# Revit family: EVID-S10.1D
name_source: partatom
category: Communication Devices
revit_build: Autodesk Revit 2017 (Build: 20160225_1515(x64)
units: mm (PartAtom-declared; Revit-internal decimal feet)

## family parameters
Always vertical = Yes
Cut with Voids When Loaded = No
Maintain Annotation Orientation = Yes
OmniClass Number = 23.85.10.11.11.21
OmniClass Title = Speakers
Part Type = Normal
Room Calculation Point = No
Round Connector Dimension = Use Diameter
Shared = No
Work Plane-Based = Yes

## types (2) — shared parameters
ArchitectsAndEngineersSpecs = https://www.electrovoice.com
Depth = 490.8 mm  [stored 1.61024 ft]
Description = Two 10 inch high-excursion woofers. Carefully engineered for outdoor environments (IP54 nad IP65), without compromising performance. 400 W power handling provides for 120 dB maximum SPL (126 dB peak). 70/100 V transformer input panel accessory available. Crossover input panel accessory available.
Disclaimer = http://resource.boschsecurity.com
Height = 360.5 mm  [stored 1.18274 ft]
IfcExportAs = IfcBuildingElementProxy
IfcExportType = IfcBuildingElementProxyType
InstallationManual = https://www.electrovoice.com
Length = 650.7 mm  [stored 2.13484 ft]
Manufacturer = Electro Voice
ManufacturerURL = https://www.electrovoice.com
PlanningTools = https://www.electrovoice.com
ProductInformation = https://www.electrovoice.com
Uniclass2015Code = Pr_60_75_08_02
Version = 1
zero-valued in all types: Default Elevation

## per-type parameters (varying)
| type | CTN | GrillMaterial | LoudspeakerMaterial | MaterialRALColour | ModelNumber |
| EVIDS10.1DB_Subwoofer_2x10"_Cabinet_Black | EVIDS10.1DB | 16GA Powder-coatedGalvanneal - B | 13-plyWeather-resistantBirchEVCoat -RAL9004 | RAL9004 | F.01U.332.744 |
| EVIDS10.1DW_Subwoofer_2x10"_Cabinet_White | EVIDS10.1DW | 16GA Powder-coatedGalvanneal - W | 13-plyWeather-resistantBirchEVCoat -RAL9003 | RAL9003 | F.01U.332.745 |

note: [stored X ft] marks values corroborated as IEEE doubles in the binary element streams (Revit-internal decimal feet)

## geometry (parser evidence)
native form markers: Blend x2, Sweep x7
no freeform markers — native parametric forms only
